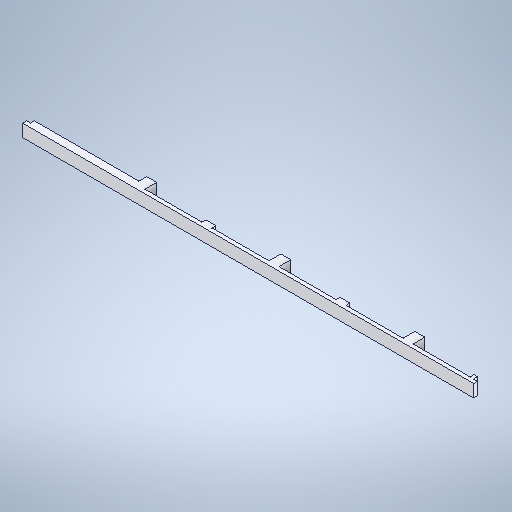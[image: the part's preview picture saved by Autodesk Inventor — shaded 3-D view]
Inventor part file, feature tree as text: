
AUTODESK INVENTOR PART (.ipt)
format: ipt  version: 2025 (Build 290162000, 162)  size: 644,608 bytes
history: native  units: in
note: dims shown in document units (in); Inventor stores cm internally (conversion verified against a paired STEP export)
features: projected_geometry x12, sketch x9, extrude x6
ambient origin geometry x8: Origin, YZ Plane, XZ Plane, XY Plane, X Axis, Y Axis, Z Axis, Center Point
bodies: Solid1 (feature_tree)
feature tree (27):
  extrude  "Extrusion1"  Depth=0.25in
  extrude  "Extrusion2"  Depth=0.875in
  extrude  "Extrusion3"  Depth=1.3375in
  extrude  "Extrusion4"  Depth=9.0in
  extrude  "Extrusion5"  Depth=0.0787in TaperAngle=0.0deg
  sketch  "Sketch7"  dims[d50=0.1in]
  extrude  "Extrusion6"  Depth=0.1in
  sketch  "Sketch1"  dims[d0=0.25in d1=0.25in]
  sketch  "Sketch Rectangular Pattern1"  dims[d2=0.9375in d3=0.875in]
  sketch  "Sketch3"  dims[d4=0.2in d5=1.9685in d7=1.3375in d8=0.7874in d10=1.325in]
  projected_geometry  "Projected Loop2"
  sketch  "Sketch Rectangular Pattern3"  dims[d13=2.75in d16=9.0in]
  projected_geometry  "Projected Loop3"
  sketch  "Sketch4"  dims[d17=2.75in d33=0.0787in d34=0.0in]
  projected_geometry  "Projected Loop4"
  sketch  "Sketch5"  dims[d42=0.125in d43=0.125in d44=0.125in d45=0.125in d48=0.1in]
  projected_geometry  "Projected Loop5"
  sketch  "Sketch6"  dims[d49=0.1in]
  projected_geometry  "Projected Loop6"
  projected_geometry  "Projected Loop7"
  projected_geometry  "Projected Loop8"
  projected_geometry  "Projected Loop9"
  projected_geometry  "Projected Loop10"
  projected_geometry  "Projected Loop11"
  projected_geometry  "Projected Loop12"
  projected_geometry  "Projected Loop13"
  sketch  "Sketch8"  dims[d51=0.1in d52=0.1in d53=0.1in d54=0.1in d55=0.1in d56=0.1in d57=0.1in d58=0.515in d59=0.5575in d60=1.1811in d62=0.75in d63=0.3937in d65=1.0in d67=0.1in d68=0.1in d69=0.1in d70=0.1in d71=0.1in d72=0.1in d73=0.0787in d74=0.0in d75=0.0787in d76=0.0787in d77=0.0787in d78=0.0in d79=0.0787in d80=0.0787in d81=0.0787in d82=0.0in d83=0.5in d84=0.4in d85=0.2in d86=0.4in d87=0.1575in d88=0.0787in d89=0.0in d90=0.0in d91=1.2875in d92=2.475in d93=2.475in d94=2.5in d95=0.0in]
